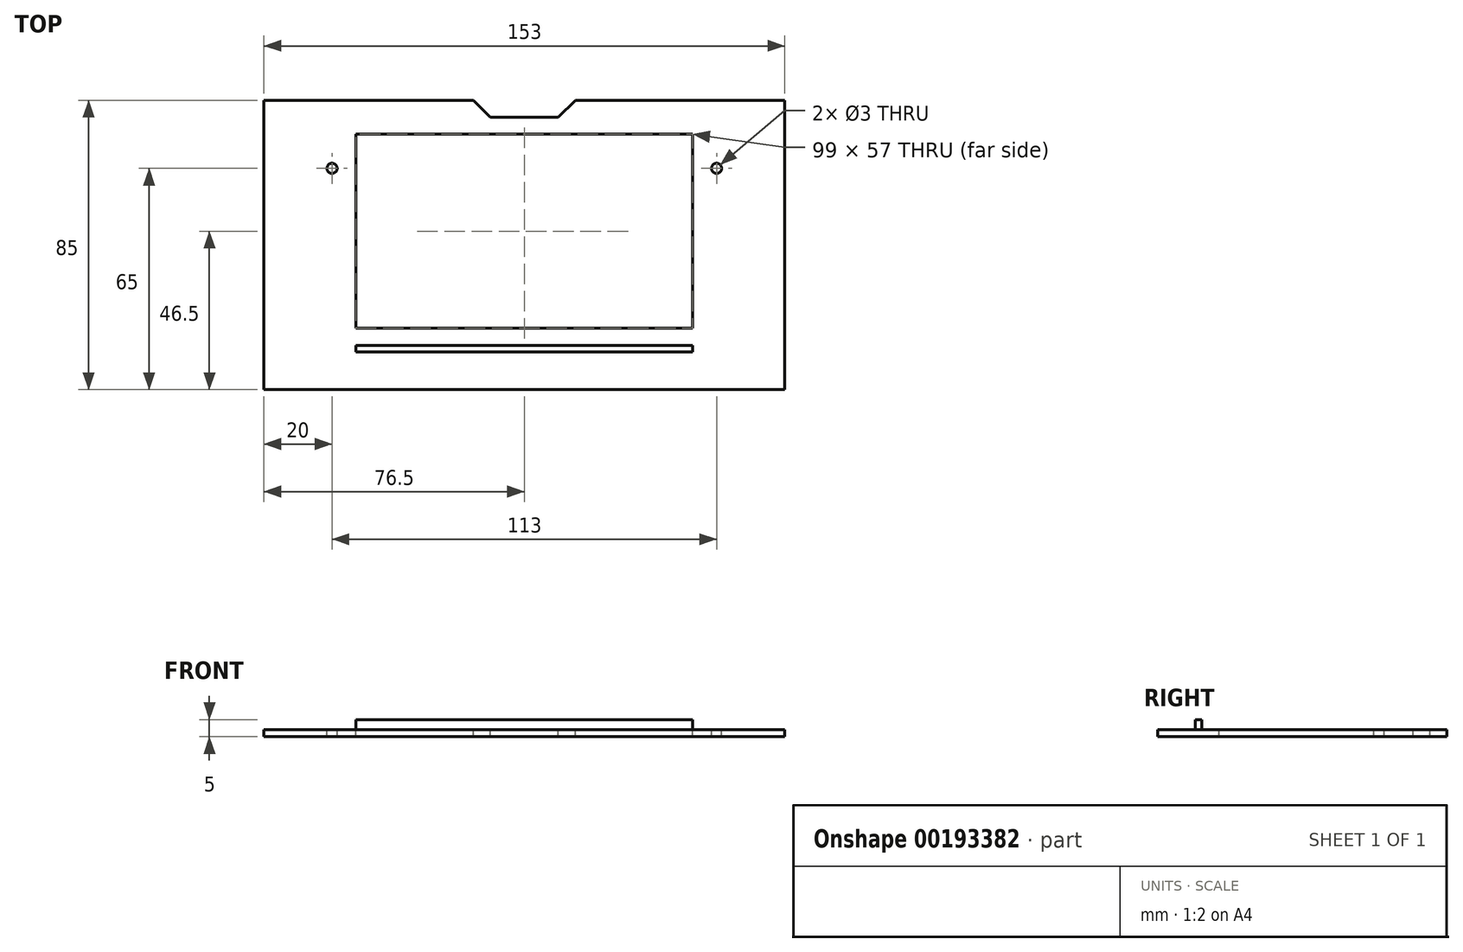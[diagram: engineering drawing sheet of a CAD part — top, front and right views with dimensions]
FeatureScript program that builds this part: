
annotation { "Feature Type Name" : "Feature", "Feature Type Description" : "" }
export const myFeature = defineFeature(function(context is Context, id is Id, definition is map)
    precondition{}
    {
        {
            var Q0;
            Q0=qCreatedBy(makeId("Top.planeOp"),FACE);
            var sketch = newSketch(context, id + "F0", { "sketchPlane" : qUnion([Q0])});
            skLineSegment(sketch, "E0.bottom", {"start": v(-76.5, 42.5) * mm, "end": v(-15, 42.5) * mm});
            skLineSegment(sketch, "E0.top", {"start": v(-76.5, -42.5) * mm, "end": v(76.5, -42.5) * mm});
            skLineSegment(sketch, "E0.left", {"start": v(-76.5, 42.5) * mm, "end": v(-76.5, -42.5) * mm});
            skLineSegment(sketch, "E0.right", {"start": v(76.5, 42.5) * mm, "end": v(76.5, -42.5) * mm});
            skLineSegment(sketch, "E1", {"start": v(-76.5, 42.5) * mm, "end": v(76.5, -42.5) * mm, "construction": true});
            skLineSegment(sketch, "E2.bottom", {"start": v(-49.5, 32.5) * mm, "end": v(49.5, 32.5) * mm});
            skLineSegment(sketch, "E2.top", {"start": v(-49.5, -24.5) * mm, "end": v(49.5, -24.5) * mm});
            skLineSegment(sketch, "E2.left", {"start": v(-49.5, 32.5) * mm, "end": v(-49.5, -24.5) * mm});
            skLineSegment(sketch, "E2.right", {"start": v(49.5, 32.5) * mm, "end": v(49.5, -24.5) * mm});
            skLineSegment(sketch, "E3", {"start": v(-49.5, -24.5) * mm, "end": v(-76.5, -24.5) * mm, "construction": true});
            skLineSegment(sketch, "E4", {"start": v(49.5, -24.5) * mm, "end": v(76.5, -24.5) * mm, "construction": true});
            skLineSegment(sketch, "E5", {"start": v(0, 37.5) * mm, "end": v(0, -42.5) * mm, "construction": true});
            skLineSegment(sketch, "E6", {"start": v(-15, 42.5) * mm, "end": v(-10, 37.5) * mm});
            skLineSegment(sketch, "E7", {"start": v(-10, 37.5) * mm, "end": v(10, 37.5) * mm});
            skLineSegment(sketch, "E8", {"start": v(10, 37.5) * mm, "end": v(15, 42.5) * mm});
            skLineSegment(sketch, "E9.trimOffspring", {"start": v(15, 42.5) * mm, "end": v(76.5, 42.5) * mm});
            skCircle(sketch, "E10", {"center": v(-56.5, 22.5) * mm, "radius": 1.5 * mm});
            skCircle(sketch, "E11", {"center": v(56.5, 22.5) * mm, "radius": 1.5 * mm});
            skLineSegment(sketch, "E12", {"start": v(-56.5, 22.5) * mm, "end": v(56.5, 22.5) * mm, "construction": true});
            skPoint(sketch, "E13", {"position": v(0, 22.5) * mm});
            skLineSegment(sketch, "E14.bottom", {"start": v(-49.5, -29.5) * mm, "end": v(49.5, -29.5) * mm, "construction": true});
            skLineSegment(sketch, "E14.top", {"start": v(-49.5, -31.5) * mm, "end": v(49.5, -31.5) * mm, "construction": true});
            skLineSegment(sketch, "E14.left", {"start": v(-49.5, -29.5) * mm, "end": v(-49.5, -31.5) * mm, "construction": true});
            skLineSegment(sketch, "E14.right", {"start": v(49.5, -29.5) * mm, "end": v(49.5, -31.5) * mm, "construction": true});
            skSolve(sketch);
        }
        {
            var Q0;
            Q0=makeQuery(id+"F0.imprint","IMPRINT",FACE,{"disambiguationData":[TD([[makeQuery(id+"F0.imprint","IMPRINT",EDGE,{"derivedFrom":sQuery(id+"F0.wireOp",EDGE,"E0.bottom")}),-1.0]])]});
            extrude(context, id + "F1", {"entities" : qUnion([Q0]), "oppositeDirection" : true, "depth" : 2 * mm});
        }
        {
            var Q0;
            Q0=makeQuery(id+"F0.imprint","IMPRINT",FACE,{"disambiguationData":[TD([[makeQuery(id+"F0.imprint","IMPRINT",EDGE,{"derivedFrom":sQuery(id+"F0.wireOp",EDGE,"E0.bottom")}),-1.0]])]});
            var sketch = newSketch(context, id + "F2", { "sketchPlane" : qUnion([Q0])});
            skLineSegment(sketch, "E15.0", {"start": v(-49.5, -31.5) * mm, "end": v(49.5, -31.5) * mm});
            skLineSegment(sketch, "E15.1", {"start": v(-49.5, -29.5) * mm, "end": v(49.5, -29.5) * mm});
            skLineSegment(sketch, "E15.2", {"start": v(-49.5, -29.5) * mm, "end": v(-49.5, -31.5) * mm});
            skLineSegment(sketch, "E15.3", {"start": v(49.5, -29.5) * mm, "end": v(49.5, -31.5) * mm});
            skSolve(sketch);
        }
        {
            var Q0;
            Q0 = qSketchRegion(id + "F2", true);
            extrude(context, id + "F3", {"entities" : qUnion([Q0]), "operationType" : NewBodyOperationType.ADD, "depth" : 3 * mm});
        }
    });
